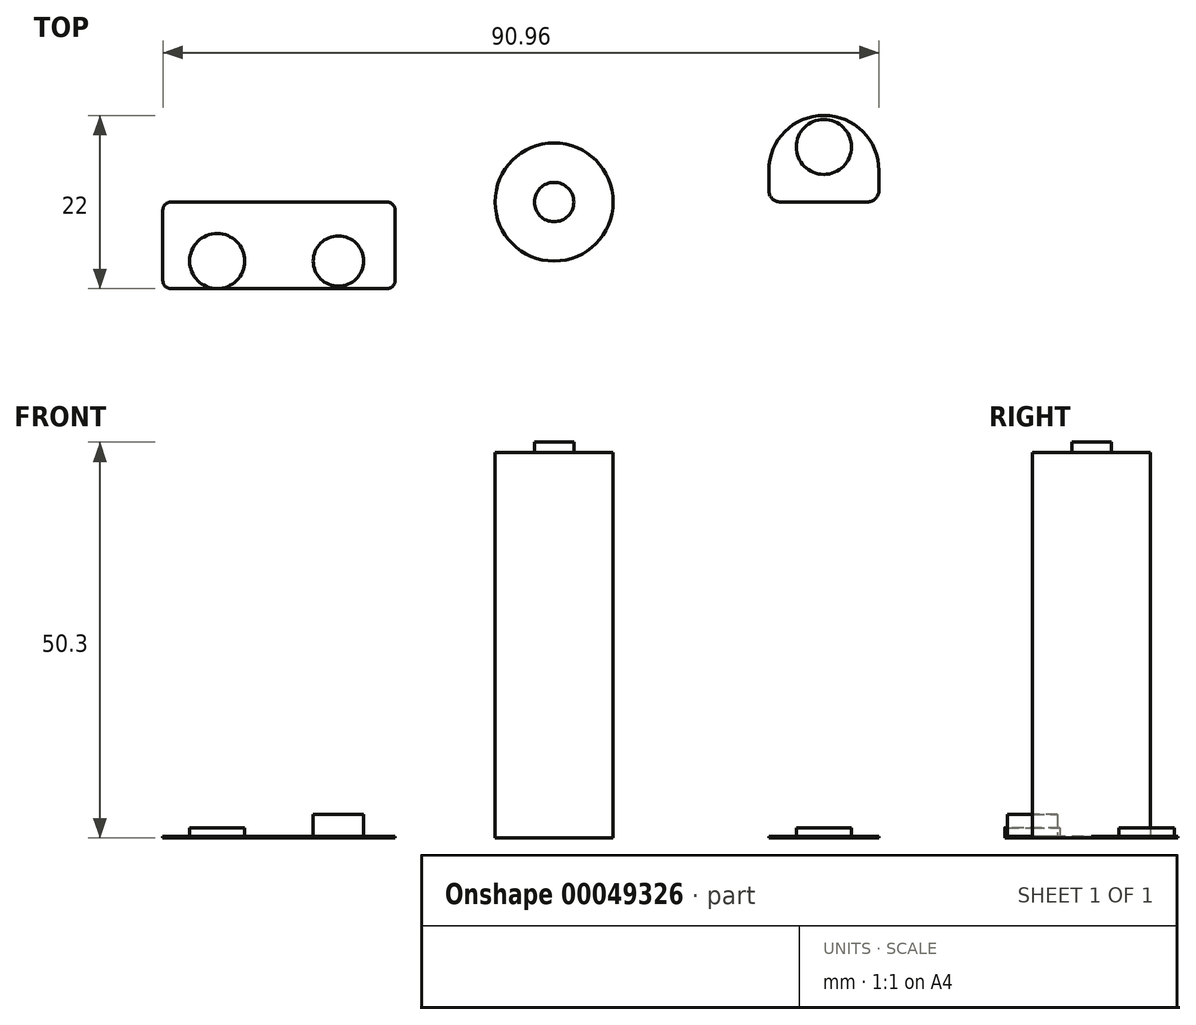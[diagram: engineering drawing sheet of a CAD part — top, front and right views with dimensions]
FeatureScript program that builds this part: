
annotation { "Feature Type Name" : "Feature", "Feature Type Description" : "" }
export const myFeature = defineFeature(function(context is Context, id is Id, definition is map)
    precondition{}
    {
        {
            var Q0;
            Q0=qCreatedBy(makeId("Top.planeOp"),FACE);
            var sketch = newSketch(context, id + "F0", { "sketchPlane" : qUnion([Q0])});
            skCircle(sketch, "E0", {"center": v(0, 0) * mm, "radius": 7.5 * mm});
            skLineSegment(sketch, "E1.bottom", {"start": v(-48.7, 0) * mm, "end": v(-21.2, 0) * mm});
            skLineSegment(sketch, "E1.top", {"start": v(-48.7, -11) * mm, "end": v(-21.2, -11) * mm});
            skLineSegment(sketch, "E1.left", {"start": v(-49.7, -1) * mm, "end": v(-49.7, -10) * mm});
            skLineSegment(sketch, "E1.right", {"start": v(-20.2, -1) * mm, "end": v(-20.2, -10) * mm});
            skPoint(sketch, "E2.visualSharp", {"position": v(-20.2, -11) * mm});
            skArc(sketch, "E2.filletArc", {"start": v(-21.2, -11) * mm, "mid": v(-20.5, -10.7) * mm, "end": v(-20.2, -10) * mm});
            skPoint(sketch, "E3.visualSharp", {"position": v(-49.7, 0) * mm});
            skArc(sketch, "E3.filletArc", {"start": v(-48.7, 0) * mm, "mid": v(-49.41, -0.3) * mm, "end": v(-49.7, -1) * mm});
            skPoint(sketch, "E4.visualSharp", {"position": v(-20.2, 0) * mm});
            skArc(sketch, "E4.filletArc", {"start": v(-20.2, -1) * mm, "mid": v(-20.5, -0.3) * mm, "end": v(-21.2, 0) * mm});
            skPoint(sketch, "E5.visualSharp", {"position": v(-49.7, -11) * mm});
            skArc(sketch, "E5.filletArc", {"start": v(-49.7, -10) * mm, "mid": v(-49.41, -10.7) * mm, "end": v(-48.7, -11) * mm});
            skCircle(sketch, "E6", {"center": v(-42.8, -7.5) * mm, "radius": 3.5 * mm});
            skCircle(sketch, "E7", {"center": v(-27.4, -7.5) * mm, "radius": 3.2 * mm});
            skLineSegment(sketch, "E8", {"start": v(-49.7, -7.5) * mm, "end": v(-39.3, -7.5) * mm, "construction": true});
            skLineSegment(sketch, "E9", {"start": v(-40.29, -7.5) * mm, "end": v(-20.2, -7.5) * mm, "construction": true});
            skLineSegment(sketch, "E10.bottom", {"start": v(27.26, 4) * mm, "end": v(41.26, 4) * mm, "construction": true});
            skLineSegment(sketch, "E10.top", {"start": v(28.76, 0) * mm, "end": v(39.76, 0) * mm});
            skLineSegment(sketch, "E10.left", {"start": v(27.26, 4) * mm, "end": v(27.26, 1.5) * mm});
            skLineSegment(sketch, "E10.right", {"start": v(41.26, 4) * mm, "end": v(41.26, 1.5) * mm});
            skArc(sketch, "E11", {"start": v(41.26, 4) * mm, "mid": v(34.26, 11) * mm, "end": v(27.26, 4) * mm});
            skLineSegment(sketch, "E12.bottom", {"start": v(32.76, 0) * mm, "end": v(35.76, 0) * mm});
            skLineSegment(sketch, "E12.top", {"start": v(32.76, -3.5) * mm, "end": v(35.76, -3.5) * mm, "construction": true});
            skLineSegment(sketch, "E12.left", {"start": v(32.76, 0) * mm, "end": v(32.76, -3.5) * mm});
            skLineSegment(sketch, "E12.right", {"start": v(35.76, 0) * mm, "end": v(35.76, -3.5) * mm});
            skArc(sketch, "E13", {"start": v(32.76, -3.5) * mm, "mid": v(34.26, -5) * mm, "end": v(35.76, -3.5) * mm});
            skLineSegment(sketch, "E14", {"start": v(34.26, 4) * mm, "end": v(34.26, -3.5) * mm, "construction": true});
            skPoint(sketch, "E15.endSnap0", {"position": v(34.26, -5) * mm});
            skLineSegment(sketch, "E16", {"start": v(32.76, -5) * mm, "end": v(35.76, -5) * mm, "construction": true});
            skPoint(sketch, "E17.visualSharp", {"position": v(27.26, 0) * mm});
            skArc(sketch, "E17.filletArc", {"start": v(27.26, 1.5) * mm, "mid": v(27.7, 0.44) * mm, "end": v(28.76, 0) * mm});
            skPoint(sketch, "E18.visualSharp", {"position": v(41.26, 0) * mm});
            skArc(sketch, "E18.filletArc", {"start": v(39.76, 0) * mm, "mid": v(40.82, 0.44) * mm, "end": v(41.26, 1.5) * mm});
            skCircle(sketch, "E19", {"center": v(34.26, 7) * mm, "radius": 3.5 * mm});
            skCircle(sketch, "E20", {"center": v(0, 0) * mm, "radius": 2.5 * mm});
            skSolve(sketch);
        }
        {
            var Q0;
            Q0=makeQuery(id+"F0.imprint","IMPRINT",FACE,{"disambiguationData":[TD([[makeQuery(id+"F0.imprint","IMPRINT",EDGE,{"derivedFrom":sQuery(id+"F0.wireOp",EDGE,"E1.bottom")}),-1.0]])]});
            var Q1;
            Q1=makeQuery(id+"F0.imprint","IMPRINT",FACE,{"disambiguationData":[TD([[makeQuery(id+"F0.imprint","IMPRINT",EDGE,{"derivedFrom":sQuery(id+"F0.wireOp",EDGE,"E6")}),1.0]])]});
            var Q2;
            Q2=makeQuery(id+"F0.imprint","IMPRINT",FACE,{"disambiguationData":[TD([[makeQuery(id+"F0.imprint","IMPRINT",EDGE,{"derivedFrom":sQuery(id+"F0.wireOp",EDGE,"E7")}),1.0]])]});
            extrude(context, id + "F1", {"entities" : qUnion([Q0, Q1, Q2]), "depth" : 0.2 * mm});
        }
        {
            var Q0;
            Q0=makeQuery(id+"F0.imprint","IMPRINT",FACE,{"disambiguationData":[TD([[makeQuery(id+"F0.imprint","IMPRINT",EDGE,{"derivedFrom":sQuery(id+"F0.wireOp",EDGE,"E6")}),1.0]])]});
            extrude(context, id + "F2", {"entities" : qUnion([Q0]), "operationType" : NewBodyOperationType.ADD, "depth" : 1.3 * mm});
        }
        {
            var Q0;
            Q0=makeQuery(id+"F0.imprint","IMPRINT",FACE,{"disambiguationData":[TD([[makeQuery(id+"F0.imprint","IMPRINT",EDGE,{"derivedFrom":sQuery(id+"F0.wireOp",EDGE,"E7")}),1.0]])]});
            extrude(context, id + "F3", {"entities" : qUnion([Q0]), "operationType" : NewBodyOperationType.ADD, "depth" : 3 * mm});
        }
        {
            var Q0;
            Q0=makeQuery(id+"F0.imprint","IMPRINT",FACE,{"disambiguationData":[TD([[makeQuery(id+"F0.imprint","IMPRINT",EDGE,{"derivedFrom":sQuery(id+"F0.wireOp",EDGE,"E0")}),1.0]])]});
            var Q1;
            Q1=makeQuery(id+"F0.imprint","IMPRINT",FACE,{"disambiguationData":[TD([[makeQuery(id+"F0.imprint","IMPRINT",EDGE,{"derivedFrom":sQuery(id+"F0.wireOp",EDGE,"E20")}),1.0]])]});
            extrude(context, id + "F4", {"entities" : qUnion([Q0, Q1]), "depth" : 49 * mm});
        }
        {
            var Q0;
            Q0=makeQuery(id+"F0.imprint","IMPRINT",FACE,{"disambiguationData":[TD([[makeQuery(id+"F0.imprint","IMPRINT",EDGE,{"derivedFrom":sQuery(id+"F0.wireOp",EDGE,"E20")}),1.0]])]});
            extrude(context, id + "F5", {"entities" : qUnion([Q0]), "operationType" : NewBodyOperationType.ADD, "depth" : 50.3 * mm});
        }
        {
            var Q0;
            Q0=makeQuery(id+"F0.imprint","IMPRINT",FACE,{"disambiguationData":[TD([[makeQuery(id+"F0.imprint","IMPRINT",EDGE,{"derivedFrom":sQuery(id+"F0.wireOp",EDGE,"E12.bottom")}),-1.0]])]});
            var Q1;
            Q1=makeQuery(id+"F0.imprint","IMPRINT",FACE,{"disambiguationData":[TD([[makeQuery(id+"F0.imprint","IMPRINT",EDGE,{"derivedFrom":sQuery(id+"F0.wireOp",EDGE,"E10.left")}),1.0]])]});
            var Q2;
            Q2=makeQuery(id+"F0.imprint","IMPRINT",FACE,{"disambiguationData":[TD([[makeQuery(id+"F0.imprint","IMPRINT",EDGE,{"derivedFrom":sQuery(id+"F0.wireOp",EDGE,"E19")}),1.0]])]});
            extrude(context, id + "F6", {"entities" : qUnion([Q0, Q1, Q2]), "depth" : 0.2 * mm});
        }
        {
            var Q0;
            Q0=makeQuery(id+"F0.imprint","IMPRINT",FACE,{"disambiguationData":[TD([[makeQuery(id+"F0.imprint","IMPRINT",EDGE,{"derivedFrom":sQuery(id+"F0.wireOp",EDGE,"E19")}),1.0]])]});
            extrude(context, id + "F7", {"entities" : qUnion([Q0]), "operationType" : NewBodyOperationType.ADD, "depth" : 1.3 * mm});
        }
    });
